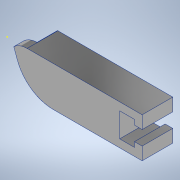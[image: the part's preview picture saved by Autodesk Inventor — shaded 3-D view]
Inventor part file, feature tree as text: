
AUTODESK INVENTOR PART (.ipt)
format: ipt  version: 2022 (Build 260153000, 153)  size: 163,328 bytes
history: native  units: mm
features: sketch x4, extrude x3, fillet x1
ambient origin geometry x8: Origin, YZ Plane, XZ Plane, XY Plane, X Axis, Y Axis, Z Axis, Center Point
bodies: Body1 (feature_tree)
feature tree (8):
  extrude  "Extrusion2"  Depth=5.8mm
  extrude  "Extrusion6"  Depth=12.0mm
  extrude  "Extrusion8"  TaperAngle=0.0deg  [1 undecoded]
  fillet  "Fillet2"  Radius=36.2mm
  sketch  "Sketch12"  dims[d85=5.6mm d86=9.5mm d87=3.0mm d89=5.0mm d90=8.0mm d91=0.0mm d92=19.198622mm d93=10.0mm d98=5.5mm d99=0.0mm d100=0.0mm d101=15.0mm]
  sketch  "Sketch5"  dims[d41=5.8mm d48=44.0mm]
  sketch  "Sketch9"  dims[d56=12.0mm d57=0.0mm d63=45.0mm]
  sketch  "Sketch11"  dims[d67=15.6mm d71=0.0mm d72=36.2mm]
note: 1 required parameter value undecoded (feature->parameter linkage not recoverable at this tier; creation-order binding heuristic only, values carry confidence <= 0.55)
